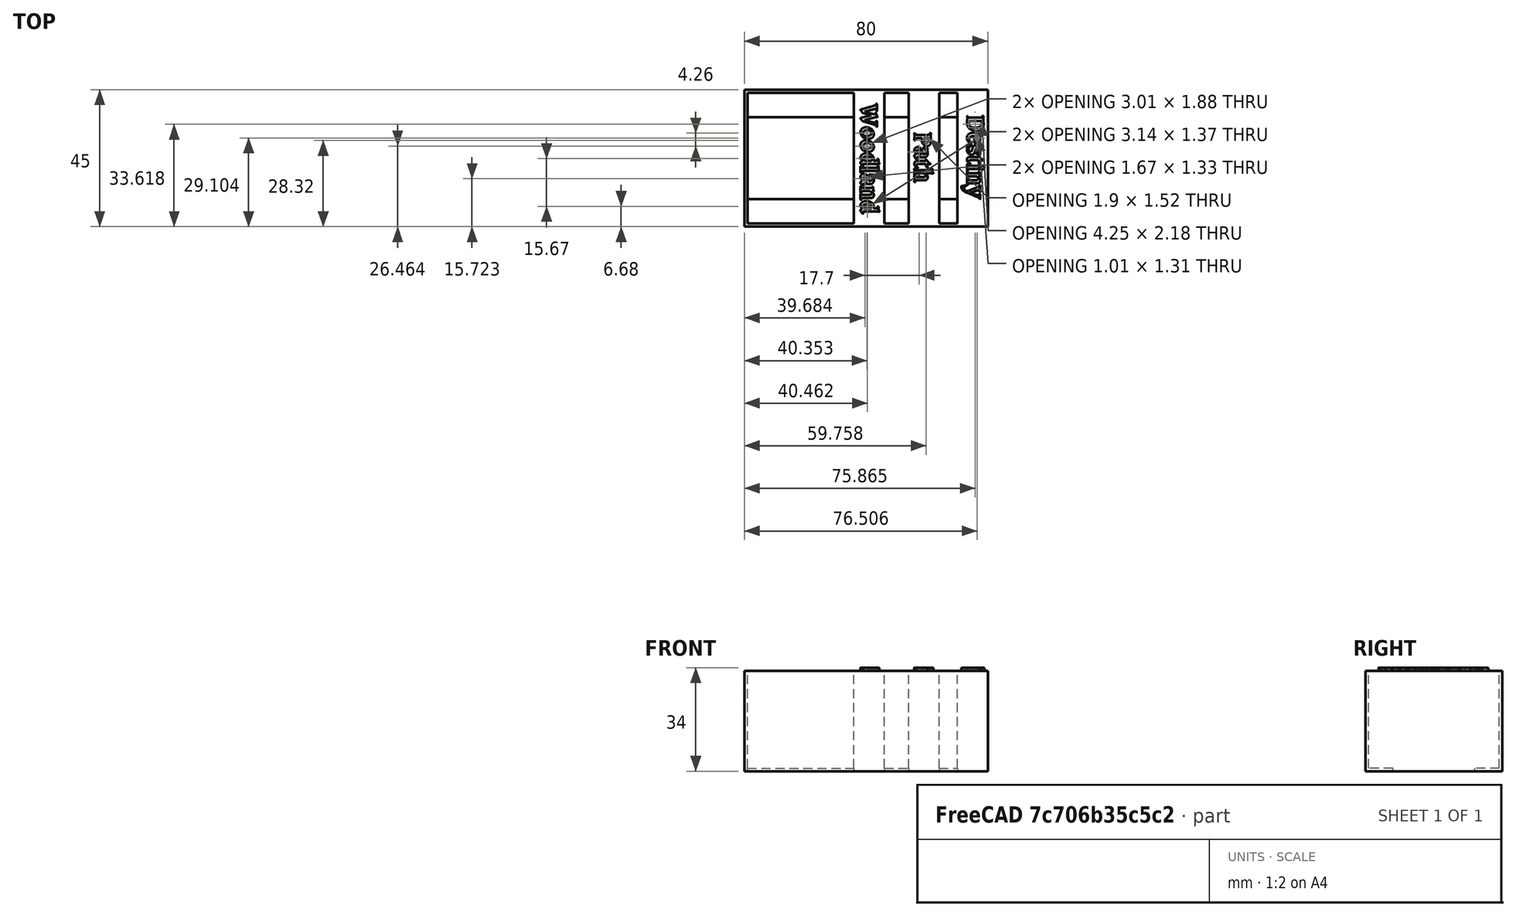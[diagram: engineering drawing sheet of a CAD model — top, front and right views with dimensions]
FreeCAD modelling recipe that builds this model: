
FCSTD DOCUMENT  (FreeCAD 0.18R4 (GitTag))
Label: woodland
License: All rights reserved
LicenseURL: http://en.wikipedia.org/wiki/All_rights_reserved
objects: Part::Box×9, Part::MultiFuse×4, Part::Part2DObjectPython×3, Part::Extrusion×3, Part::Cut×2
note: 21 computed .brp shape members not serialized (recipe doc carries the construction recipe); baked Part::Feature solids carry a one-line shape summary decoded from their .brp

FEATURE [Part::Box] Box  label="Cube"
  AttacherType = Attacher::AttachEngine3D
  Height = 33
  Length = 202
  Placement = pos=(0,-1,0) rot=(0,0,1;0rad)
  Width = 45
FEATURE [Part::Box] Box001  label="Cube001"
  AttacherType = Attacher::AttachEngine3D
  Height = 33
  Length = 200
  Placement = pos=(1,0,0) rot=(0,0,1;0rad)
  Width = 43
FEATURE [Part::Cut] Cut
  Base = -> Box
  Tool = -> Box001
FEATURE [Part::Box] Box002  label="Cube002"
  AttacherType = Attacher::AttachEngine3D
  Height = 1
  Length = 202
  Width = 8
FEATURE [Part::Box] Box003  label="Cube003"
  AttacherType = Attacher::AttachEngine3D
  Height = 1
  Length = 202
  Placement = pos=(0,35,0) rot=(0,0,1;0rad)
  Width = 8
FEATURE [Part::MultiFuse] Fusion
  Shapes = -> [Cut,Box002,Box003]
FEATURE [Part::Box] Box004  label="Cube004"
  AttacherType = Attacher::AttachEngine3D
  Height = 33
  Length = 10
  Placement = pos=(36,0,0) rot=(0,0,1;0rad)
  Width = 43
FEATURE [Part::Box] Box005  label="Cube005"
  AttacherType = Attacher::AttachEngine3D
  Height = 33
  Length = 10
  Placement = pos=(54,0,0) rot=(0,0,1;0rad)
  Width = 43
FEATURE [Part::Box] Box006  label="Cube006"
  AttacherType = Attacher::AttachEngine3D
  Height = 33
  Length = 10
  Placement = pos=(70,0,0) rot=(0,0,1;0rad)
  Width = 43
FEATURE [Part::Box] Box007  label="Cube007"
  AttacherType = Attacher::AttachEngine3D
  Height = 33
  Length = 129
  Placement = pos=(73,-1,0) rot=(0,0,1;0rad)
  Width = 45
FEATURE [Part::MultiFuse] Fusion001
  Shapes = -> [Fusion,Box004,Box005,Box006]
FEATURE [Part::Cut] Cut001
  Base = -> Fusion001
  Tool = -> Box007
FEATURE [Part::Box] Box008  label="Cube008"
  AttacherType = Attacher::AttachEngine3D
  Height = 33
  Length = 8
  Placement = pos=(72,-1,0) rot=(0,0,1;0rad)
  Width = 45
FEATURE [Part::MultiFuse] Fusion002  label="box"
  Shapes = -> [Cut001,Box008]
FEATURE [Part::Part2DObjectPython] ShapeString  # Draft 2D object (typed FeaturePython)
  FontFile = <userpath>/Downloads/talisman/Caxton Bold.otf
  Placement = pos=(38,40.34,33) rot=(0,0,-1;1.5708rad)
  Size = 3
  String = Woodland
  Tracking = 0
FEATURE [Part::Extrusion] Extrude029
  Base = -> ShapeString
  Dir = (0,0,1)
  DirMode = 2
  FaceMakerClass = Part::FaceMakerBullseye
  LengthFwd = 1
  LengthRev = 0
  Placement = pos=(0.3,-1,0) rot=(0,0,1;0rad)
  Solid = false
  Symmetric = false
FEATURE [Part::Part2DObjectPython] ShapeString001  # Draft 2D object (typed FeaturePython)
  FontFile = <userpath>/Downloads/talisman/Caxton Bold.otf
  Placement = pos=(56,35.5,33) rot=(0,0,1;0rad)
  Size = 3
  String = Path
  Tracking = 0
FEATURE [Part::Part2DObjectPython] ShapeString002  # Draft 2D object (typed FeaturePython)
  FontFile = <userpath>/Downloads/talisman/Caxton Bold.otf
  Placement = pos=(77.44,28.28,33) rot=(0,0,1;0rad)
  Size = 3
  String = Destiny
  Tracking = 0
FEATURE [Part::Extrusion] Extrude030
  Base = -> ShapeString001
  Dir = (0,0,1)
  DirMode = 2
  FaceMakerClass = Part::FaceMakerBullseye
  LengthFwd = 1
  LengthRev = 0
  Placement = pos=(20.5,86,0) rot=(0,0,-1;1.5708rad)
  Solid = false
  Symmetric = false
FEATURE [Part::Extrusion] Extrude031
  Base = -> ShapeString002
  Dir = (0,0,1)
  DirMode = 2
  FaceMakerClass = Part::FaceMakerBullseye
  LengthFwd = 1
  LengthRev = 0
  Placement = pos=(45,113,0) rot=(0,0,-1;1.5708rad)
  Solid = false
  Symmetric = false
FEATURE [Part::MultiFuse] Fusion003
  Shapes = -> [Extrude029,Extrude030,Extrude031]
